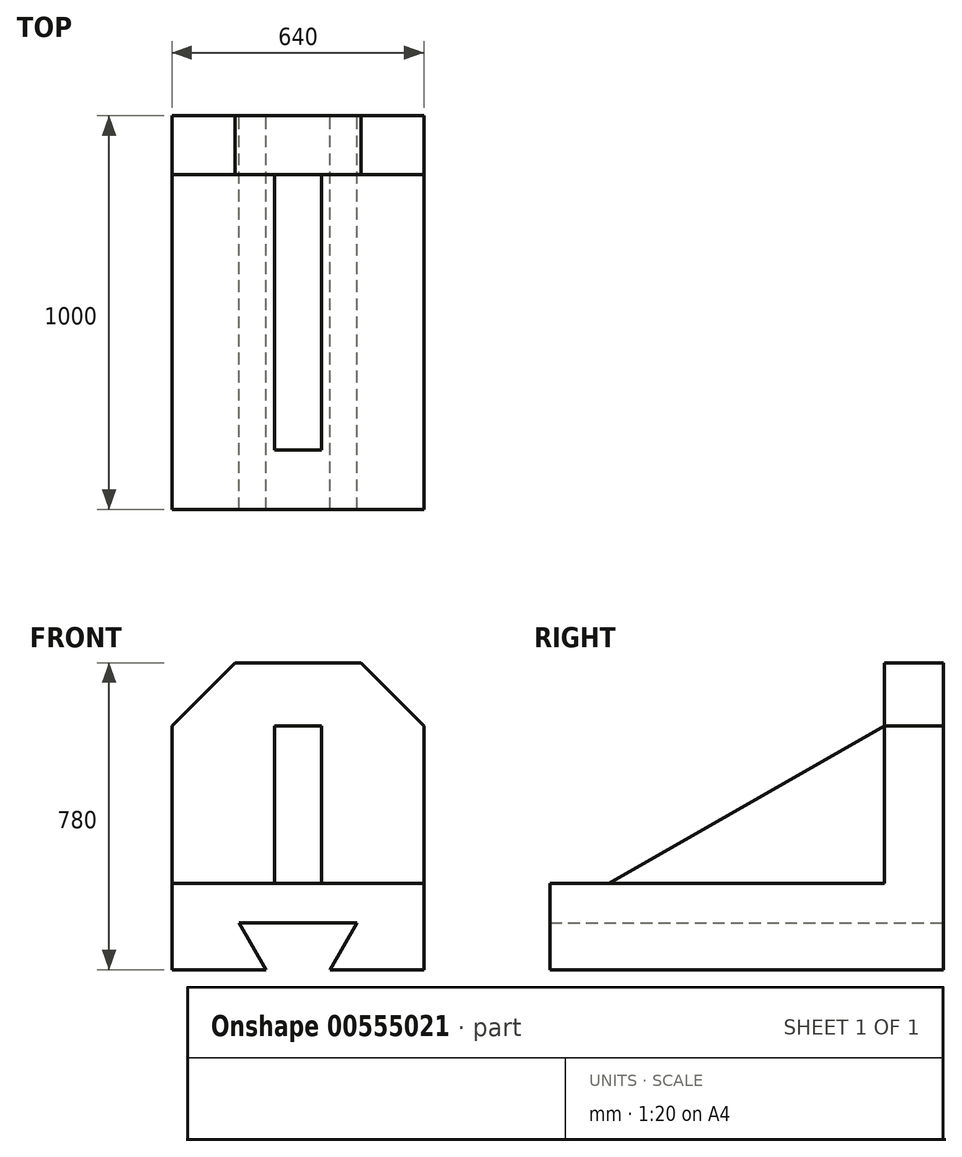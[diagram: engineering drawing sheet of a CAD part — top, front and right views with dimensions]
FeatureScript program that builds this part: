
annotation { "Feature Type Name" : "Feature", "Feature Type Description" : "" }
export const myFeature = defineFeature(function(context is Context, id is Id, definition is map)
    precondition{}
    {
        {
            var Q0;
            Q0=qCreatedBy(makeId("Front.planeOp"),FACE);
            var sketch = newSketch(context, id + "F0", { "sketchPlane" : qUnion([Q0])});
            skLineSegment(sketch, "E0.bottom", {"start": v(0, 0) * mm, "end": v(640, 0) * mm});
            skLineSegment(sketch, "E0.top", {"start": v(0, 220) * mm, "end": v(640, 220) * mm});
            skLineSegment(sketch, "E0.left", {"start": v(0, 0) * mm, "end": v(0, 220) * mm});
            skLineSegment(sketch, "E0.right", {"start": v(640, 0) * mm, "end": v(640, 220) * mm});
            skLineSegment(sketch, "E1", {"start": v(238.85, 0) * mm, "end": v(170, 119.25) * mm});
            skLineSegment(sketch, "E2", {"start": v(170, 119.25) * mm, "end": v(470, 119.25) * mm});
            skLineSegment(sketch, "E3", {"start": v(470, 119.25) * mm, "end": v(401.15, 0) * mm});
            skLineSegment(sketch, "E4.top", {"start": v(0, 620) * mm, "end": v(640, 620) * mm});
            skLineSegment(sketch, "E4.left", {"start": v(0, 220) * mm, "end": v(0, 620) * mm});
            skLineSegment(sketch, "E4.right", {"start": v(640, 220) * mm, "end": v(640, 620) * mm});
            skLineSegment(sketch, "E5", {"start": v(160, 620) * mm, "end": v(160, 780) * mm});
            skLineSegment(sketch, "E6", {"start": v(160, 780) * mm, "end": v(480, 780) * mm});
            skLineSegment(sketch, "E7", {"start": v(480, 780) * mm, "end": v(480, 620) * mm});
            skLineSegment(sketch, "E8", {"start": v(0, 620) * mm, "end": v(160, 780) * mm});
            skLineSegment(sketch, "E9", {"start": v(480, 780) * mm, "end": v(640, 620) * mm});
            skSolve(sketch);
        }
        {
            var Q0;
            {var subQ1=sQuery(id+"F0.wireOp",EDGE,"E0.left");Q0=makeQuery(id+"F0.imprint","IMPRINT",FACE,{"disambiguationData":[TD([[makeQuery(id+"F0.imprint","IMPRINT",EDGE,{"derivedFrom":subQ1}),-1.0]])]});}
            extrude(context, id + "F1", {"entities" : qUnion([Q0]), "depth" : 1000 * mm});
        }
        {
            var Q0;
            Q0=makeQuery(id+"F0.imprint","IMPRINT",FACE,{"disambiguationData":[TD([[makeQuery(id+"F0.imprint","IMPRINT",EDGE,{"derivedFrom":sQuery(id+"F0.wireOp",EDGE,"E0.top")}),1.0]])]});
            var Q1;
            {var subQ2=sQuery(id+"F0.wireOp",EDGE,"E7");Q1=makeQuery(id+"F0.imprint","IMPRINT",FACE,{"disambiguationData":[TD([[makeQuery(id+"F0.imprint","IMPRINT",EDGE,{"derivedFrom":subQ2}),1.0]])]});}
            var Q2;
            {var subQ0=sQuery(id+"F0.wireOp",EDGE,"E5");Q2=makeQuery(id+"F0.imprint","IMPRINT",FACE,{"disambiguationData":[TD([[makeQuery(id+"F0.imprint","IMPRINT",EDGE,{"derivedFrom":subQ0}),-1.0]])]});}
            var Q3;
            {var subQ2=sQuery(id+"F0.wireOp",EDGE,"E5");Q3=makeQuery(id+"F0.imprint","IMPRINT",FACE,{"disambiguationData":[TD([[makeQuery(id+"F0.imprint","IMPRINT",EDGE,{"derivedFrom":subQ2}),1.0]])]});}
            extrude(context, id + "F2", {"entities" : qUnion([Q0, Q1, Q2, Q3]), "operationType" : NewBodyOperationType.ADD, "depth" : 150 * mm});
        }
        {
            var Q0;
            Q0=makeQuery(id+"F2.opExtrude","CAP_FACE",FACE,{"disambiguationData":[OSD([sQuery(id+"F0.wireOp",EDGE,"E0.top"),sQuery(id+"F0.wireOp",EDGE,"E4.left"),sQuery(id+"F0.wireOp",EDGE,"E4.right"),sQuery(id+"F0.wireOp",EDGE,"E6"),sQuery(id+"F0.wireOp",EDGE,"E8"),sQuery(id+"F0.wireOp",EDGE,"E9")])],"isStart":false});
            var sketch = newSketch(context, id + "F3", { "sketchPlane" : qUnion([Q0])});
            skLineSegment(sketch, "E10.bottom", {"start": v(260, 220) * mm, "end": v(380, 220) * mm});
            skLineSegment(sketch, "E10.top", {"start": v(260, 620) * mm, "end": v(380, 620) * mm});
            skLineSegment(sketch, "E10.left", {"start": v(260, 220) * mm, "end": v(260, 620) * mm});
            skLineSegment(sketch, "E10.right", {"start": v(380, 220) * mm, "end": v(380, 620) * mm});
            skSolve(sketch);
        }
        {
            var Q0;
            Q0=makeQuery(id+"F3.imprint","IMPRINT",FACE,{"disambiguationData":[TD([[makeQuery(id+"F3.imprint","IMPRINT",EDGE,{"derivedFrom":sQuery(id+"F3.wireOp",EDGE,"E10.bottom")}),1.0]])]});
            extrude(context, id + "F4", {"entities" : qUnion([Q0]), "operationType" : NewBodyOperationType.ADD, "depth" : 700 * mm, "offsetDistance" : 25.4 * mm});
        }
        {
            var Q0;
            Q0=makeQuery(id+"F4.opExtrude","SWEPT_FACE",FACE,{"disambiguationData":[OSD([sQuery(id+"F3.wireOp",EDGE,"E10.right")])]});
            var sketch = newSketch(context, id + "F5", { "sketchPlane" : qUnion([Q0])});
            skLineSegment(sketch, "E11", {"start": v(-850, 220) * mm, "end": v(-150, 620) * mm});
            skSolve(sketch);
        }
        {
            var Q0;
            Q0=makeQuery(id+"F5.imprint","IMPRINT",FACE,{"disambiguationData":[TD([[makeQuery(id+"F5.imprint","IMPRINT",EDGE,{"derivedFrom":sQuery(id+"F5.wireOp",EDGE,"E11")}),1.0]])]});
            extrude(context, id + "F6", {"entities" : qUnion([Q0]), "operationType" : NewBodyOperationType.REMOVE, "oppositeDirection" : true, "depth" : 267.2 * mm, "offsetDistance" : 25.4 * mm});
        }
    });
